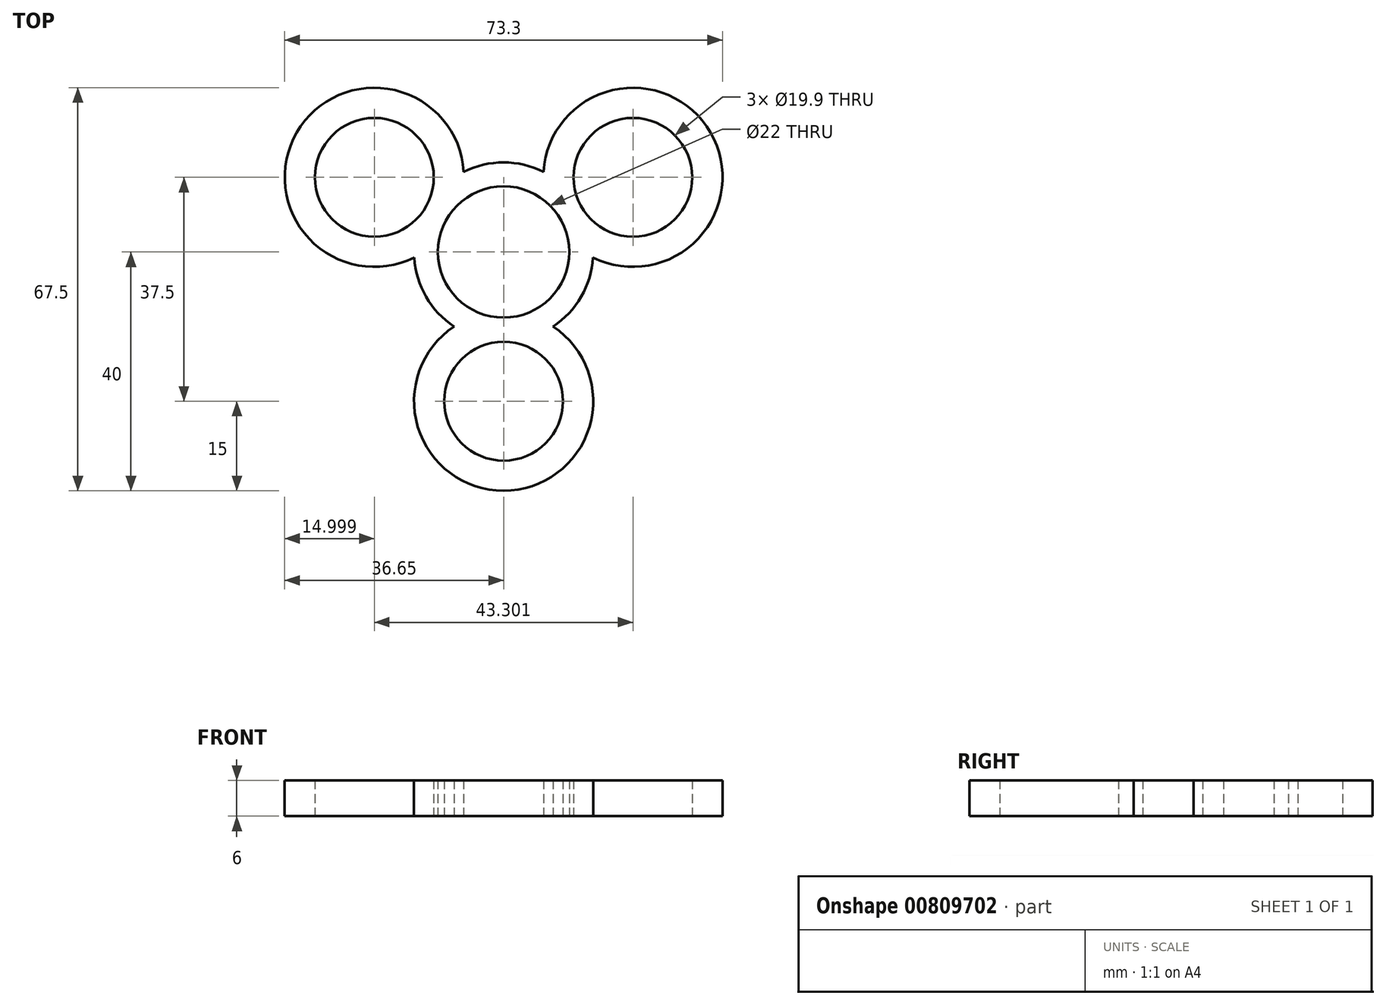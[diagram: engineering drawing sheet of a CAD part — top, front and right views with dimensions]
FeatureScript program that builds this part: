
annotation { "Feature Type Name" : "Feature", "Feature Type Description" : "" }
export const myFeature = defineFeature(function(context is Context, id is Id, definition is map)
    precondition{}
    {
        {
            var Q0;
            Q0=qCreatedBy(makeId("Top.planeOp"),FACE);
            var sketch = newSketch(context, id + "F0", { "sketchPlane" : qUnion([Q0])});
            skArc(sketch, "E0", {"start": v(-9.53, -5.5) * mm, "mid": v(0, -11) * mm, "end": v(9.53, -5.5) * mm});
            skCircle(sketch, "E1", {"center": v(0, -25) * mm, "radius": 9.95 * mm});
            skArc(sketch, "E2", {"start": v(-8.3, -12.5) * mm, "mid": v(0, -40) * mm, "end": v(8.3, -12.5) * mm});
            skArc(sketch, "E3", {"start": v(-13, -7.5) * mm, "mid": v(-10.93, -10.27) * mm, "end": v(-8.3, -12.5) * mm});
            skArc(sketch, "E4.trimOffspring", {"start": v(8.3, -12.5) * mm, "mid": v(10.93, -10.27) * mm, "end": v(13, -7.5) * mm});
            skArc(sketch, "E5.1.0", {"start": v(14.97, -0.93) * mm, "mid": v(34.64, 20) * mm, "end": v(6.68, 13.43) * mm});
            skCircle(sketch, "E5.1.1", {"center": v(21.65, 12.5) * mm, "radius": 9.95 * mm});
            skArc(sketch, "E5.1.2", {"start": v(9.53, -5.5) * mm, "mid": v(9.53, 5.5) * mm, "end": v(0, 11) * mm});
            skArc(sketch, "E5.1.3", {"start": v(6.68, 13.43) * mm, "mid": v(3.43, 14.6) * mm, "end": v(0, 15) * mm});
            skArc(sketch, "E5.1.5", {"start": v(13, -7.5) * mm, "mid": v(14.36, -4.33) * mm, "end": v(14.97, -0.93) * mm});
            skArc(sketch, "E5.2.0", {"start": v(-6.68, 13.43) * mm, "mid": v(-34.64, 20) * mm, "end": v(-14.97, -0.93) * mm});
            skCircle(sketch, "E5.2.1", {"center": v(-21.65, 12.5) * mm, "radius": 9.95 * mm});
            skArc(sketch, "E5.2.2", {"start": v(0, 11) * mm, "mid": v(-9.53, 5.5) * mm, "end": v(-9.53, -5.5) * mm});
            skArc(sketch, "E5.2.3", {"start": v(-14.97, -0.93) * mm, "mid": v(-14.36, -4.33) * mm, "end": v(-13, -7.5) * mm});
            skArc(sketch, "E5.2.5", {"start": v(0, 15) * mm, "mid": v(-3.43, 14.6) * mm, "end": v(-6.68, 13.43) * mm});
            skSolve(sketch);
        }
        {
            var Q0;
            Q0 = qSketchRegion(id + "F0", true);
            extrude(context, id + "F1", {"entities" : qUnion([Q0]), "depth" : 6 * mm, "offsetDistance" : 25 * mm});
        }
    });
